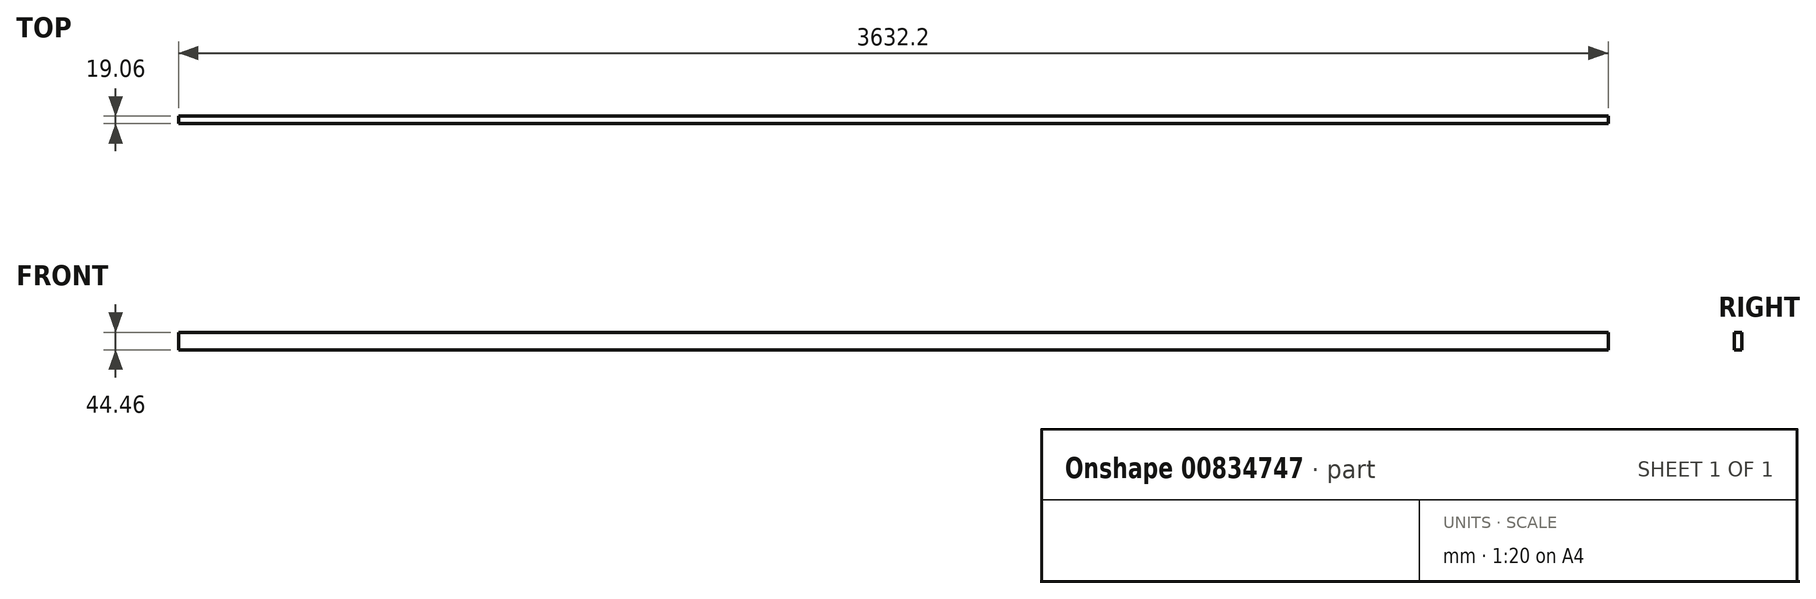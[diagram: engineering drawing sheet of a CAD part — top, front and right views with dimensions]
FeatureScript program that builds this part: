
annotation { "Feature Type Name" : "Feature", "Feature Type Description" : "" }
export const myFeature = defineFeature(function(context is Context, id is Id, definition is map)
    precondition{}
    {
        {
            var Q0;
            Q0=qCreatedBy(makeId("Front.planeOp"),FACE);
            var sketch = newSketch(context, id + "F0", { "sketchPlane" : qUnion([Q0])});
            skLineSegment(sketch, "E0.bottom", {"start": v(1816.1, -22.22) * mm, "end": v(-1816.1, -22.23) * mm});
            skLineSegment(sketch, "E0.top", {"start": v(1816.1, 22.23) * mm, "end": v(-1816.1, 22.22) * mm});
            skLineSegment(sketch, "E0.left", {"start": v(1816.1, -22.22) * mm, "end": v(1816.1, 22.23) * mm});
            skLineSegment(sketch, "E0.right", {"start": v(-1816.1, -22.23) * mm, "end": v(-1816.1, 22.22) * mm});
            skPoint(sketch, "E0.middle", {"position": v(0, 0) * mm});
            skSolve(sketch);
        }
        {
            var Q0;
            Q0=makeQuery(id+"F0.imprint","IMPRINT",FACE,{"disambiguationData":[TD([[makeQuery(id+"F0.imprint","IMPRINT",EDGE,{"derivedFrom":sQuery(id+"F0.wireOp",EDGE,"E0.bottom")}),-1.0]])]});
            extrude(context, id + "F1", {"entities" : qUnion([Q0]), "endBound" : BoundingType.SYMMETRIC, "depth" : 19.05 * mm, "offsetDistance" : 25.4 * mm});
        }
    });
